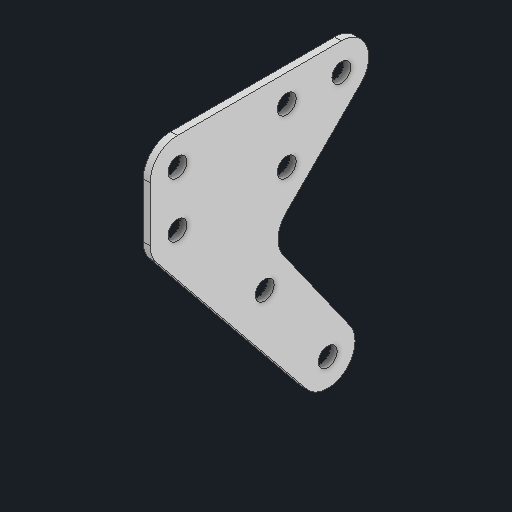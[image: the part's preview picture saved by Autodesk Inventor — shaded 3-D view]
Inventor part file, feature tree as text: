
AUTODESK INVENTOR PART (.ipt)
format: ipt  version: 2025 (Build 290162000, 162)  size: 121,344 bytes
history: native  units: in
note: dims shown in document units (in); Inventor stores cm internally (conversion verified against a paired STEP export)
features: other x3, extrude x1, sketch x1
ambient origin geometry x8: Origin, YZ Plane, XZ Plane, XY Plane, X Axis, Y Axis, Z Axis, Center Point
bodies: Solid1 (feature_tree)
feature tree (5):
  other  "Blocks"
  extrude  "Extrusion1"  Depth=0.0625in TaperAngle=0.0deg
  sketch  "Sketch1"  dims[d0=0.5in d1=0.5in d4=0.25in d5=0.5in d6=0.172in d7=0.0625in d8=0.0in]
  other  "maiin"
  other  "maiin:1"
